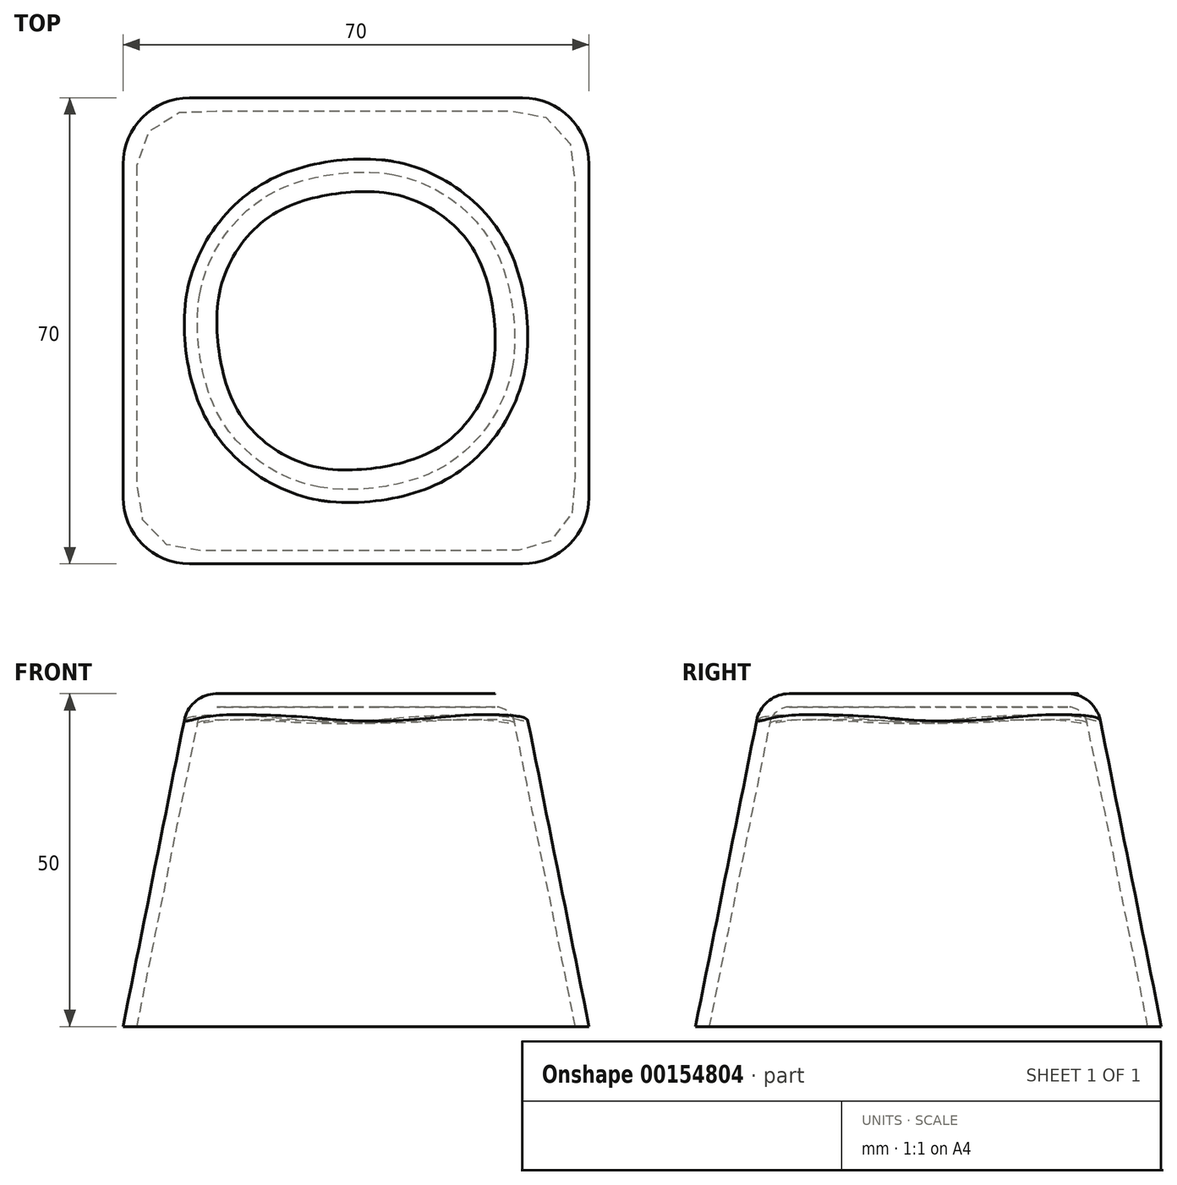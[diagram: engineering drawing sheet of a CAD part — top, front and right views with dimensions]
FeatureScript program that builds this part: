
annotation { "Feature Type Name" : "Feature", "Feature Type Description" : "" }
export const myFeature = defineFeature(function(context is Context, id is Id, definition is map)
    precondition{}
    {
        {
            var Q0;
            Q0=qCreatedBy(makeId("Top.planeOp"),FACE);
            var sketch = newSketch(context, id + "F0", { "sketchPlane" : qUnion([Q0])});
            skLineSegment(sketch, "E0.bottom", {"start": v(-25, 35) * mm, "end": v(25, 35) * mm});
            skLineSegment(sketch, "E0.top", {"start": v(-25, -35) * mm, "end": v(25, -35) * mm});
            skLineSegment(sketch, "E0.left", {"start": v(-35, 25) * mm, "end": v(-35, -25) * mm});
            skLineSegment(sketch, "E0.right", {"start": v(35, 25) * mm, "end": v(35, -25) * mm});
            skPoint(sketch, "E1.visualSharp", {"position": v(-35, 35) * mm});
            skArc(sketch, "E1.filletArc", {"start": v(-25, 35) * mm, "mid": v(-32.07, 32.07) * mm, "end": v(-35, 25) * mm});
            skPoint(sketch, "E2.visualSharp", {"position": v(35, 35) * mm});
            skArc(sketch, "E2.filletArc", {"start": v(35, 25) * mm, "mid": v(32.07, 32.07) * mm, "end": v(25, 35) * mm});
            skPoint(sketch, "E3.visualSharp", {"position": v(35, -35) * mm});
            skArc(sketch, "E3.filletArc", {"start": v(25, -35) * mm, "mid": v(32.07, -32.07) * mm, "end": v(35, -25) * mm});
            skPoint(sketch, "E4.visualSharp", {"position": v(-35, -35) * mm});
            skArc(sketch, "E4.filletArc", {"start": v(-35, -25) * mm, "mid": v(-32.07, -32.07) * mm, "end": v(-25, -35) * mm});
            skSolve(sketch);
        }
        {
            var Q0;
            Q0=qCreatedBy(makeId("Top.planeOp"),FACE);
            cPlane(context, id + "F1", {"entities" : qUnion([Q0]), "cplaneType" : CPlaneType.OFFSET, "offset" : 50 * mm, "width" : 150 * mm, "height" : 150 * mm});
        }
        {
            var Q0;
            Q0=qCreatedBy(id+"F1.planeOp",FACE);
            var sketch = newSketch(context, id + "F2", { "sketchPlane" : qUnion([Q0])});
            skCircle(sketch, "E5", {"center": v(0, 0) * mm, "radius": 25 * mm});
            skSolve(sketch);
        }
        {
            var Q0;
            Q0=makeQuery(id+"F0.imprint","IMPRINT",FACE,{"disambiguationData":[TD([[makeQuery(id+"F0.imprint","IMPRINT",EDGE,{"derivedFrom":sQuery(id+"F0.wireOp",EDGE,"E0.bottom")}),-1.0]])]});
            var Q1;
            Q1=makeQuery(id+"F2.imprint","IMPRINT",FACE,{"disambiguationData":[TD([[makeQuery(id+"F2.imprint","IMPRINT",EDGE,{"derivedFrom":sQuery(id+"F2.wireOp",EDGE,"E5")}),1.0]])]});
            loft(context, id + "F3", {"sheetProfilesArray" : [{ "sheetProfileEntities" : qUnion([Q0]) }, { "sheetProfileEntities" : qUnion([Q1]) }]});
        }
        {
            var Q0;
            Q0=makeQuery(id+"F3.opLoft","MID_CAP_EDGE",EDGE,{"disambiguationData":[OSD([sQuery(id+"F0.wireOp",EDGE,"E0.top"),sQuery(id+"F0.wireOp",EDGE,"E3.filletArc"),sQuery(id+"F0.wireOp",EDGE,"E4.filletArc"),sQuery(id+"F2.wireOp",EDGE,"E5")])],"capPos":1.0});
            fillet(context, id + "F4", {"entities" : qUnion([Q0]), "radius" : 5 * mm, "tangentPropagation" : true, "allowEdgeOverflow" : false});
        }
        {
            var Q0;
            Q0=makeQuery(id+"F3.opLoft","CAP_FACE",FACE,{"disambiguationData":[OSD([makeQuery(id+"F0.imprint","IMPRINT",FACE,{"disambiguationData":[TD([[makeQuery(id+"F0.imprint","IMPRINT",EDGE,{"derivedFrom":sQuery(id+"F0.wireOp",EDGE,"E0.bottom")}),-1.0]])]})])],"isStart":true});
            shell(context, id + "F5", {"entities" : qUnion([Q0]), "thickness" : 2 * mm});
        }
    });
